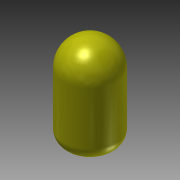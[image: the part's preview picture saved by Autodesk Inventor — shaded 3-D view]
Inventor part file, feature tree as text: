
AUTODESK INVENTOR PART (.ipt)
format: ipt  version: 2015 (Build 190159000, 159)  size: 112,128 bytes
history: native  units: in
note: dims shown in document units (in); Inventor stores cm internally (conversion verified against a paired STEP export)
features: fillet x2, extrude x1, sketch x1
ambient origin geometry x8: Origin, YZ Plane, XZ Plane, XY Plane, X Axis, Y Axis, Z Axis, Center Point
bodies: Solid1 (feature_tree)
feature tree (4):
  extrude  "Extrusion1"  Depth=0.25in TaperAngle=0.0deg
  fillet  "Fillet1"  Radius=0.5in
  fillet  "Fillet2"  Radius=0.25in
  sketch  "Sketch1"  dims[d0=1.0in d1=1.75in d2=0.0in d3=0.5in d4=0.25in]
